# Revit family: Difusores cerrados para aplicaciones generales
name_source: partatom
category: Rociadores
revit_build: Autodesk Revit 2017 (Build: 20160225_1515(x64)
units: mm (PartAtom-declared; Revit-internal decimal feet)

## family parameters
Compartido = No
Corte con vacíos al cargar = No
Cota de conector redondo = Radio de uso
Mantener orientación de anotación = No
Número OmniClass = 23.65.70.17.11.24
Punto de cálculo de habitación = No
Se basa en plano de trabajo = Sí
Siempre vertical = Sí
Tipo de pieza = Normal
Título OmniClass = Fire Fighting Sprinkler Heads

## types (2) — shared parameters
120 = Sí
Clase de presión = Norma
Cobertura = Norma
Descripción = Cabeza nebulizadora cerrada con bulbo térmico (fusible) que rompe a 57º y abre las toberas. Van equipadas con 5 o 7 toberas montadas en un ángulo de apertura de 120º y un rango de caudales suficiente para cubrir una amplia gama de necesidades.
Elevación por defecto = 1219 mm
Fabricante = Aguilera Electrónica
Flujo máximo = 25.5 L/min
Orificio = Norma
Respuesta = Norma
Símbolo = Sí
Símbolo texto modelo = Sí
URL = http://aguilera.es
Zona de acción = Sí
Ángulo = 120.00°

## per-type parameters (varying)
| type | Flujo | Flujo mínimo | Modelo |
| Difusor cerrado 5 toberas 120º -  2,4 a 25,5 l/min | 2.4 L/min | 2.4 L/min | AN/CC120T5 |
| Difusor cerrado 7 toberas 120º -  2,8 a 35,7 l/min | 2.0 L/min | 2.0 L/min | AN/CC120T7 |
